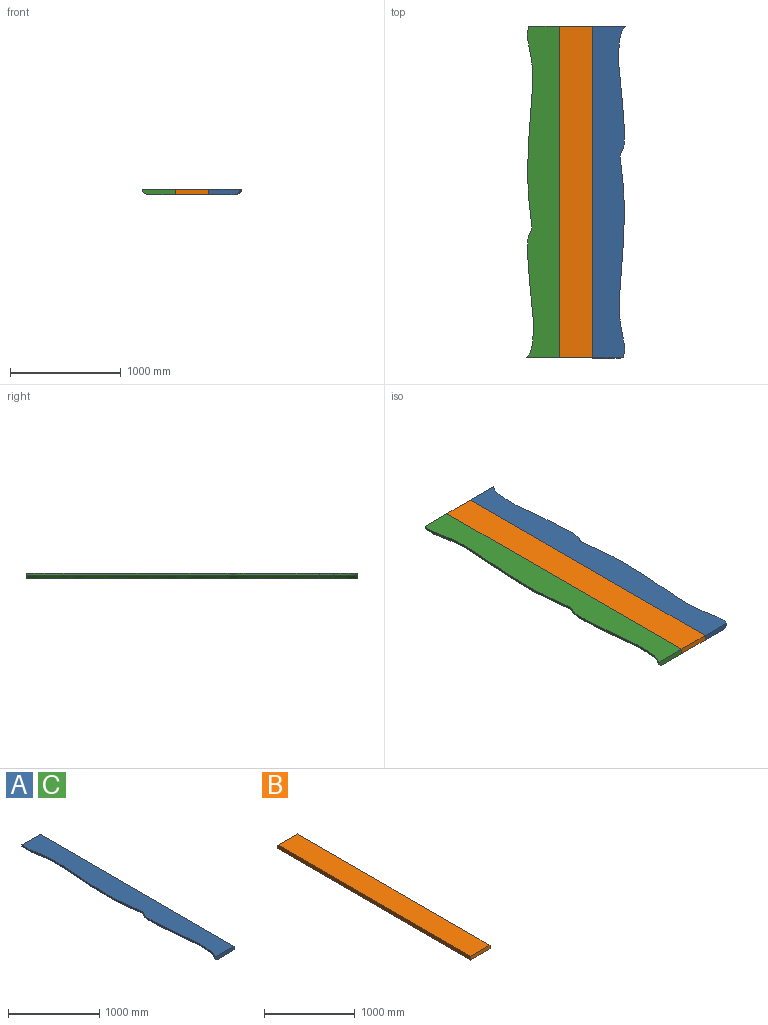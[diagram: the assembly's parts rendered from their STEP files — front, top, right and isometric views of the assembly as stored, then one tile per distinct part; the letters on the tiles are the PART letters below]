
ASSEMBLY  parts=3 mates=3
PART A: 11 faces, bbox 310.8x3062.6x56.3 mm
  f0: extruded ~2652.25x52.6mm, area 53361.2mm2, adj f1,f5,f6,f8
  f1: plane 127.7x20mm, normal (-1,0,0), area 2554.1mm2, adj f0,f2,f6,f9
  f2: extruded ~220.05x63.81mm, area 4688mm2, adj f1,f3,f6,f10
  f3: plane 303.71x53.71mm, normal (0,-1,0), area 14414.1mm2, adj f2,f4,f6,f7,f10
  f4: plane 3000x50mm, normal (1,0,0), area 150000mm2, adj f3,f5,f6,f7
  f5: plane 278.9x50mm, normal (0,1,0), area 13487.3mm2, adj f0,f4,f6,f7,f8
  f6: plane 3000x300.67mm, normal (0,0,1), area 796297.9mm2, adj f0,f1,f2,f3,f4,f5
  f7: plane 3006.32x267.55mm, normal (0,0,-1), area 705462.5mm2, adj f3,f4,f5,f8,f9,f10
  f8: bspline ~2687.85x82.92mm, area 113019.5mm2, adj f0,f5,f7,f9
  f9: plane 128.99x30mm, normal (-0.71,0,-0.71), area 5445.2mm2, adj f1,f7,f8,f10
  f10: bspline ~247.96x98.41mm, area 9852.7mm2, adj f2,f3,f7,f9
PART B: 6 faces, bbox 300x3000x50 mm
  f0: plane 300x50mm, normal (0,1,0), area 15000mm2, adj f1,f3,f4,f5
  f1: plane 3000x50mm, normal (-1,0,0), area 150000mm2, adj f0,f2,f4,f5
  f2: plane 300x50mm, normal (0,-1,0), area 15000mm2, adj f1,f3,f4,f5
  f3: plane 3000x50mm, normal (1,0,0), area 150000mm2, adj f0,f2,f4,f5
  f4: plane 3000x300mm, normal (0,0,1), area 900000mm2, adj f0,f1,f2,f3
  f5: plane 3000x300mm, normal (0,0,-1), area 900000mm2, adj f0,f1,f2,f3
PART C: same geometry as A
PLACE A rot(axis=(0,0,-1),180deg) t=(-660.85,1140.97,0)mm
PLACE B at identity
PLACE C t=(-1268.4,-1146.98,0)mm
MATE planar C.f4 <-> B.f1  axis (1,0,0) through (-1114.62,-3.01,25)mm
MATE cylindrical A.f6 <-> A.f4  axis (0,0,1) through (-681.32,-12.66,50)mm
MATE parallel A.f4 <-> B.f3  axis (-1,0,0) through (-814.62,-3.01,25)mm
